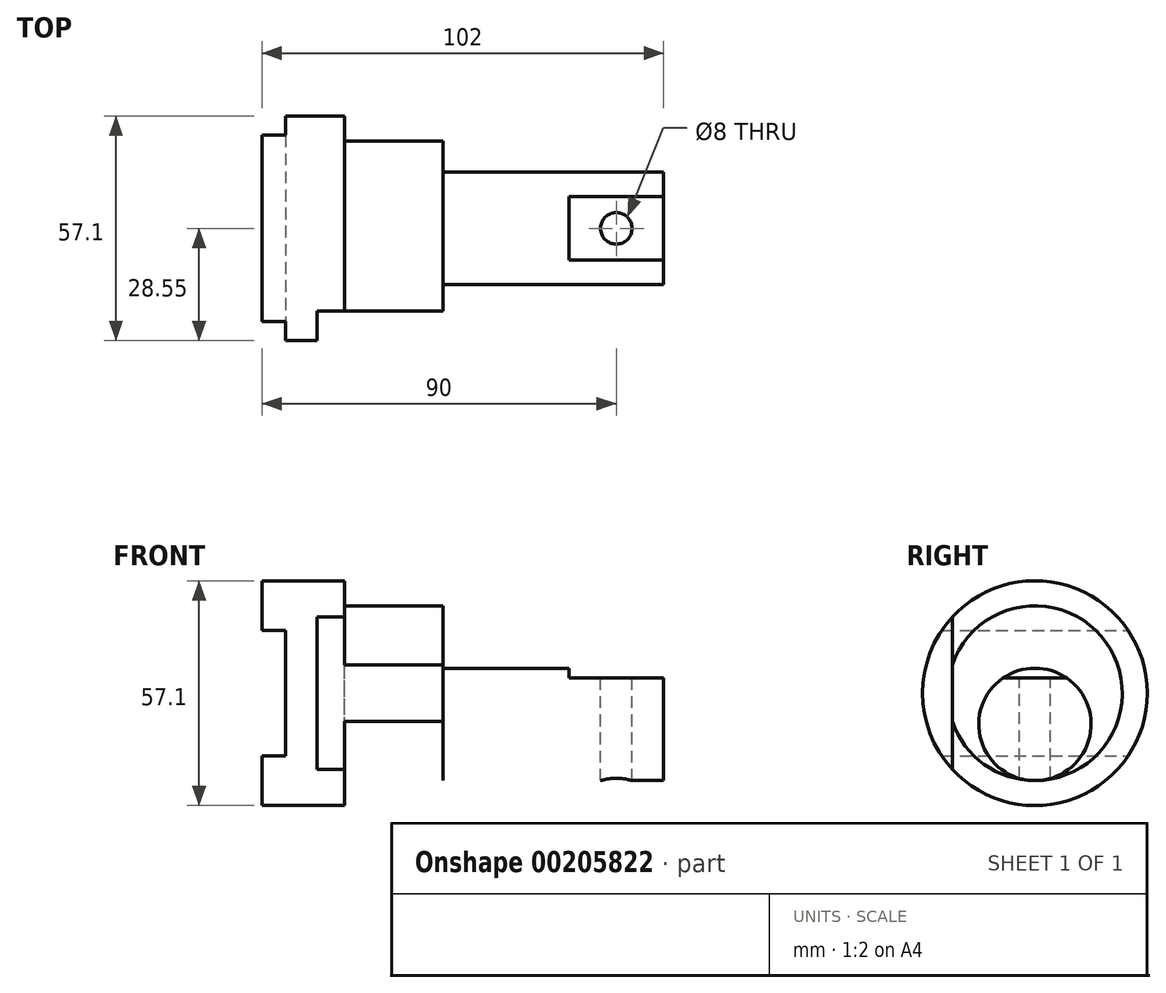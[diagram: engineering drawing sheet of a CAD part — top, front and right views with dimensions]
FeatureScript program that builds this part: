
annotation { "Feature Type Name" : "Feature", "Feature Type Description" : "" }
export const myFeature = defineFeature(function(context is Context, id is Id, definition is map)
    precondition{}
    {
        {
            var Q0;
            Q0=qCreatedBy(makeId("Right.planeOp"),FACE);
            var sketch = newSketch(context, id + "F0", { "sketchPlane" : qUnion([Q0])});
            skCircle(sketch, "E0", {"center": v(0, 0) * mm, "radius": 28.55 * mm});
            skCircle(sketch, "E1", {"center": v(0, 0) * mm, "radius": 22.2 * mm});
            skCircle(sketch, "E2", {"center": v(0, -7.93) * mm, "radius": 14.28 * mm});
            skSolve(sketch);
        }
        {
            var Q0;
            Q0=makeQuery(id+"F0.imprint","IMPRINT",FACE,{"disambiguationData":[TD([[makeQuery(id+"F0.imprint","IMPRINT",EDGE,{"derivedFrom":sQuery(id+"F0.wireOp",EDGE,"E2")}),1.0]])]});
            extrude(context, id + "F1", {"entities" : qUnion([Q0]), "depth" : 102 * mm});
        }
        {
            var Q0;
            Q0=qCreatedBy(makeId("Right.planeOp"),FACE);
            var sketch = newSketch(context, id + "F2", { "sketchPlane" : qUnion([Q0])});
            skCircle(sketch, "E3.0.0", {"center": v(0, 0) * mm, "radius": 22.2 * mm});
            skSolve(sketch);
        }
        {
            var Q0;
            Q0=makeQuery(id+"F2.imprint","IMPRINT",FACE,{"disambiguationData":[TD([[makeQuery(id+"F2.imprint","IMPRINT",EDGE,{"derivedFrom":sQuery(id+"F2.wireOp",EDGE,"E3.0.0")}),1.0]])]});
            extrude(context, id + "F3", {"entities" : qUnion([Q0]), "operationType" : NewBodyOperationType.ADD, "depth" : (25 + 21) * mm});
        }
        {
            var Q0;
            Q0=makeQuery(id+"F0.imprint","IMPRINT",FACE,{"disambiguationData":[TD([[makeQuery(id+"F0.imprint","IMPRINT",EDGE,{"derivedFrom":sQuery(id+"F0.wireOp",EDGE,"E0")}),1.0]])]});
            extrude(context, id + "F4", {"entities" : qUnion([Q0]), "operationType" : NewBodyOperationType.ADD, "depth" : 21 * mm});
        }
        {
            var Q0;
            Q0=qCreatedBy(makeId("Front.planeOp"),FACE);
            cPlane(context, id + "F5", {"entities" : qUnion([Q0]), "cplaneType" : CPlaneType.OFFSET, "offset" : 42.7 * mm, "width" : 150 * mm, "height" : 150 * mm});
        }
        {
            var Q0;
            Q0=qCreatedBy(id+"F5.planeOp",FACE);
            var sketch = newSketch(context, id + "F6", { "sketchPlane" : qUnion([Q0])});
            skLineSegment(sketch, "E4.bottom", {"start": v(78, 23) * mm, "end": v(119.97, 23) * mm});
            skLineSegment(sketch, "E4.top", {"start": v(78, 3.85) * mm, "end": v(119.97, 3.85) * mm});
            skLineSegment(sketch, "E4.left", {"start": v(78, 23) * mm, "end": v(78, 3.85) * mm});
            skLineSegment(sketch, "E4.right", {"start": v(119.97, 23) * mm, "end": v(119.97, 3.85) * mm});
            skLineSegment(sketch, "E5.0.0", {"start": v(102, 6.35) * mm, "end": v(102, -22.2) * mm, "construction": true});
            skLineSegment(sketch, "E6", {"start": v(46, 6.35) * mm, "end": v(102, 6.35) * mm, "construction": true});
            skLineSegment(sketch, "E7", {"start": v(102, -22.2) * mm, "end": v(46, -22.2) * mm, "construction": true});
            skSolve(sketch);
        }
        {
            var Q0;
            Q0=makeQuery(id+"F6.imprint","IMPRINT",FACE,{"disambiguationData":[TD([[makeQuery(id+"F6.imprint","IMPRINT",EDGE,{"derivedFrom":sQuery(id+"F6.wireOp",EDGE,"E4.bottom")}),-1.0]])]});
            extrude(context, id + "F7", {"entities" : qUnion([Q0]), "operationType" : NewBodyOperationType.REMOVE, "endBound" : BoundingType.THROUGH_ALL, "oppositeDirection" : true, "depth" : 25 * mm});
        }
        {
            var Q0;
            Q0=makeQuery(id+"F7.boolean.opBoolean","COPY",FACE,{"derivedFrom":makeQuery(id+"F7.opExtrude","SWEPT_FACE",FACE,{"disambiguationData":[OSD([sQuery(id+"F6.wireOp",EDGE,"E4.top")])]})});
            var sketch = newSketch(context, id + "F8", { "sketchPlane" : qUnion([Q0])});
            skPoint(sketch, "E8", {"position": v(90, 0) * mm});
            skSolve(sketch);
        }
        {
            var Q0;
            Q0=sQuery(id+"F8.wireOp",VERTEX,"E8");
            var Q1;
            Q1=makeQuery(id+"F1.opExtrude","SWEPT_BODY",BODY,{"disambiguationData":[OSD([sQuery(id+"F0.wireOp",EDGE,"E2")])]});
            hole(context, id + "F9", {"style" : HoleStyle.SIMPLE, "endStyle" : HoleEndStyle.THROUGH, "holeDiameter" : 8 * mm, "isTappedThrough" : true, "tappedDepth" : 12 * mm, "tapClearance" : 3, "locations" : qUnion([Q0]), "scope" : qUnion([Q1])});
        }
        {
            var Q0;
            Q0=qCreatedBy(id+"F5.planeOp",FACE);
            var sketch = newSketch(context, id + "F10", { "sketchPlane" : qUnion([Q0])});
            skLineSegment(sketch, "E9", {"start": v(0, 28.55) * mm, "end": v(21, 28.55) * mm, "construction": true});
            skLineSegment(sketch, "E10", {"start": v(21, -28.55) * mm, "end": v(0, -28.55) * mm, "construction": true});
            skLineSegment(sketch, "E11.0", {"start": v(0, 28.55) * mm, "end": v(0, -28.55) * mm, "construction": true});
            skLineSegment(sketch, "E12.bottom", {"start": v(-6, -16) * mm, "end": v(6, -16) * mm});
            skLineSegment(sketch, "E12.top", {"start": v(-6, 16) * mm, "end": v(6, 16) * mm});
            skLineSegment(sketch, "E12.left", {"start": v(-6, -16) * mm, "end": v(-6, 16) * mm});
            skLineSegment(sketch, "E12.right", {"start": v(6, -16) * mm, "end": v(6, 16) * mm});
            skPoint(sketch, "E12.middle", {"position": v(0, 0) * mm});
            skSolve(sketch);
        }
        {
            var Q0;
            Q0=makeQuery(id+"F10.imprint","IMPRINT",FACE,{"disambiguationData":[TD([[makeQuery(id+"F10.imprint","IMPRINT",EDGE,{"derivedFrom":sQuery(id+"F10.wireOp",EDGE,"E12.bottom")}),1.0]])]});
            extrude(context, id + "F11", {"entities" : qUnion([Q0]), "operationType" : NewBodyOperationType.REMOVE, "endBound" : BoundingType.THROUGH_ALL, "oppositeDirection" : true, "depth" : 25 * mm});
        }
        {
            var Q0;
            Q0=qCreatedBy(makeId("Top.planeOp"),FACE);
            cPlane(context, id + "F12", {"entities" : qUnion([Q0]), "cplaneType" : CPlaneType.OFFSET, "offset" : 54 * mm, "width" : 150 * mm, "height" : 150 * mm});
        }
        {
            var Q0;
            Q0=qCreatedBy(id+"F12.planeOp",FACE);
            var sketch = newSketch(context, id + "F13", { "sketchPlane" : qUnion([Q0])});
            skLineSegment(sketch, "E13", {"start": v(21, 22.2) * mm, "end": v(46, 22.2) * mm, "construction": true});
            skLineSegment(sketch, "E14", {"start": v(46, -22.2) * mm, "end": v(21, -22.2) * mm, "construction": true});
            skLineSegment(sketch, "E15.bottom", {"start": v(14, -41.24) * mm, "end": v(58.32, -41.24) * mm});
            skLineSegment(sketch, "E15.top", {"start": v(14, -21) * mm, "end": v(58.32, -21) * mm});
            skLineSegment(sketch, "E15.left", {"start": v(14, -41.24) * mm, "end": v(14, -21) * mm});
            skLineSegment(sketch, "E15.right", {"start": v(58.32, -41.24) * mm, "end": v(58.32, -21) * mm});
            skLineSegment(sketch, "E16", {"start": v(7.18, 0) * mm, "end": v(82.11, 0) * mm, "construction": true});
            skSolve(sketch);
        }
        {
            var Q0;
            Q0=makeQuery(id+"F13.imprint","IMPRINT",FACE,{"disambiguationData":[TD([[makeQuery(id+"F13.imprint","IMPRINT",EDGE,{"derivedFrom":sQuery(id+"F13.wireOp",EDGE,"E15.bottom")}),1.0]])]});
            extrude(context, id + "F14", {"entities" : qUnion([Q0]), "operationType" : NewBodyOperationType.REMOVE, "endBound" : BoundingType.THROUGH_ALL, "oppositeDirection" : true, "depth" : 25 * mm});
        }
    });
